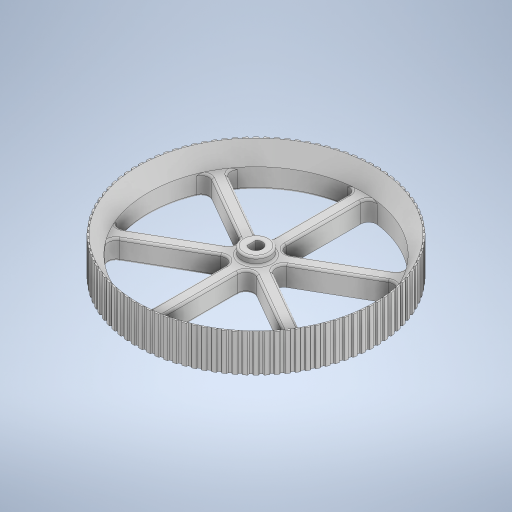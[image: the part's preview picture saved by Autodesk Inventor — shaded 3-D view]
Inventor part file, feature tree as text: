
AUTODESK INVENTOR PART (.ipt)
format: ipt  version: 2024.2 (Build 282272000, 272)  size: 1,080,832 bytes
history: native  units: mm
features: sketch x3, extrude x3, fillet x2, revolve x1
ambient origin geometry x8: Origin, YZ Plane, XZ Plane, XY Plane, X Axis, Y Axis, Z Axis, Center Point
bodies: Solid1 (feature_tree)
feature tree (9):
  revolve  "Revolution1"  [1 undecoded]
  sketch  "Sketch3"  dims[d2=5.0mm d3=30.0mm]
  extrude  "Extrusion1"  Depth=30.0mm
  extrude  "Extrusion2"  Depth=0.5mm
  extrude  "Extrusion3"  Depth=0.5mm
  fillet  "Fillet1"  Radius=10.0mm
  fillet  "Fillet2"  Radius=7.0mm
  sketch  "Sketch2"  dims[d0=3.0mm d1=10.0mm]
  sketch  "Sketch4"  dims[d4=360.0deg d5=3.2mm d6=1.15mm d7=10.0mm d8=7.0mm d9=3.0mm d10=1.5mm d11=60.0mm d13=360.0deg d15=5.0mm d16=0.0mm d17=7.0mm d18=0.0mm d19=120.0deg d20=120.0deg d21=1.6mm d22=1.0mm d23=0.5mm d24=1000.0mm d26=360.0deg d28=0.0mm d29=0.0mm d30=2.0mm d31=0.5mm d32=1.6mm d33=120.0deg d34=120.0deg d35=1.0mm d36=0.5mm]
note: 1 required parameter value undecoded (feature->parameter linkage not recoverable at this tier; creation-order binding heuristic only, values carry confidence <= 0.55)
